# Revit family: Gira_230266
name_source: partatom
category: Electrical Fixtures
revit_build: Autodesk Revit 2017 (Build: 20160225_1515(x64)
units: mm (PartAtom-declared; Revit-internal decimal feet)

## family parameters
Cut with Voids When Loaded = No
Host = Face
Maintain Annotation Orientation = Yes
Part Type = Normal
Room Calculation Point = No
Round Connector Dimension = Use Diameter
Shared = No

## types (1)
- Auto.ctrl.sw. 2 Komfort 2.20 m Gira TX_44 p.white
    Animal zone = No
    Available = No
    BIM (1) = https://media.stage.bim.site
    Category = Sensor element for movement sensor
    Colour = White
    Constant light control = No
    Creep-under protection = No
    Data sheet (1) = https://katalog.gira.de
    Default Elevation = 1219 mm
    Description = ACS 2 Kmf.2.20m TX_44 PW,System  2000 automatic control switch 2 Komfort top unit, mounting height up to 2.20 m,Komfort top unit,pure white,Automatic control switch for switching light automatically, depending on the movement of heat and ambient brightness.,,Features:,- Extension of the detection range in combination with an auxiliary insert for presence detectors and automatic control switches.,- Teach-in function for adapting the brightness threshold.,- Switch-on brightness can be saved permanently, with dimming insert.,- Can be dimmed slightly, with dimming insert and connected auxiliary insert.,- Crawl-under protection.,- Delay time limit.,- IR remote control for setting various functions.,- Dimming function, with dimming insert.,- Short-term operation, e.g. for controlling acoustic signal transmitters, with switching insert.,- Display LED.,- Occupied-home simulation.,- Nightlight function.,- Motion detection which can be toggled between the indoors and outdoors.,,Notes :,- For operation with System 2000 flush-mounted insert for dimming, switching, or auxiliary insert use for presence detectors and automatic control switches.
    Detection angle horizontal = 1 - 180
    Dim function with dimmer basic element = Yes
    GTIN = 4010337104742
    HAN = 230266
    HVAC-control = No
    Halogen free = No
    HeinzeBIM = https://bimportal.heinze.de
    Manufacturer = Gira
    Manufacturer URL = https://www.gira.de
    Material = Other
    Material quality = Other
    Max. duty cycle = 1800
    Max. transmission range frontally = 12
    Max. transmission range sideways = 6
    Min. switch-on time = 10
    Model = Movement sensor
    Mounting height = 2.2
    Mounting method = Flush mounted (plaster)
    Name = Auto.ctrl.sw. 2 Komfort 2.20 m Gira TX_44 p.white
    Networkable = No
    RAL-number (akin) = 9010
    Response value luminosity adjustable = No
    Response value sensitivity adjustable = Yes
    Staircase monitoring = Yes
    Suitable for degree of protection (IP) = IP20
    Suitable for wireless transmission = No
    URL = http://katalog.gira.de

## geometry (parser evidence)
native form markers: Sweep x2
no freeform markers — native parametric forms only
